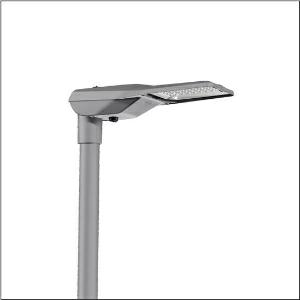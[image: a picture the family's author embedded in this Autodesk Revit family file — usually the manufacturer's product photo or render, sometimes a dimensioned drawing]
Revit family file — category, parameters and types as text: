
# Revit family: streetlight_sl_21_iq_mini___st1_0a_5xe2d41y08jb_7656
name_source: partatom
category: Lighting Fixtures
units: mm (PartAtom-declared; Revit-internal decimal feet)

## family parameters
Cut with Voids When Loaded = No
Host = Face
Light Source = No
Part Type = Normal
Room Calculation Point = No
Round Connector Dimension = Use Diameter
Shared = No

## types (1)
- --- (1 x LED, 11600 lm, 72.5 W, 4000K)
    Apparent Load = 73 VA
    CIE Flux Codes = 40 73 97 100 100
    Color Rendering = 70
    Color Temperature = 4000K
    Default Elevation = 1800 mm
    Description = Streetlight SL 21 iQ mini, mast luminaire, primary light control with lens, of PMMA, primary optical cover: cover, of toughened safety glass, transparent, light distribution: ST1.0a, light emission: direct distribution, primary light characteristic: asymmetric, installation type: post-top, side-entry, LED, High Power LED, rated luminous flux: 11.600lm, luminous efficacy: 160lm/W, light colour: 740, colour temperature: 4000K, control: presetting dimming logarithmic, Street-Remote, Auto-Match, Temp-Guard, Lumen-Switch, Night-Set, Smart-Wire, Light-Fading, Desk-Remote (wireless, voltage-free reading and setting of iQ features in the workshop via application-optimized NFC function/RFID function), optimised constant luminous flux control (CLO 2.0), mains connection: 220..240V, AC, 50/60Hz, start of lifetime: 73W, end of service life: 76W, reduction: 33W, luminaire housing, of diecast aluminium, powder-coated, Siteco® metallic grey (DB 702S), corrosivity category C5 mid according to DIN EN ISO 12944, please order mast flange separately, inclination adjustable: 0°, 5°, 10°, 15°, sealing non-destructively replaceable, multi-level sealing system, length: 628mm, width: 235mm, height: 110mm, mast flange for spigot size: 42mm (side-entry): 5XC10008XM4, 60/48mm (side-entry/post-top): 5XC10108XM2, 76/60mm (side-entry/post-top): 5XC10108XM1, Smart Interface below and above, protection rating (complete): IP66, insulation class (complete): insulation class II (safety insulation), certification: CE, ENEC, ENEC+, VDE, impact resistance: IK09, permissible operating ambient temperature for outdoor applications: -40..+50°C, standard-compliant lighting for roads and squares, packaging unit: 1 piece

Light Distribution: ST1.0a
    Height = 110 mm
    Lamp = 1 x LED
    Lamp Light Flux = 11600 lm
    Lamp Power = 72.5 W
    Lamp count = 1
    Length = 625 mm
    Luminous efficacy = 160 lm/W
    Manufacturer = Siteco
    ModVariant = No
    Model = 5XE2D41Y08JB
    Number of Poles = 1
    OnlyDefault = Yes
    Power Factor = 1
    Product Name = Streetlight SL 21 iQ mini | ST1.0a
    Product group = mast luminaire | pylon top
    ProductGroupID = 6100
    Protection Class = Protection class II
    Protection Degree = IP 66
    RLX_Detail_Level = 1
    RLX_Emergency_Light_Flux = 0 lm
    RLX_Emergency_Type = 0
    RLX_Emergency_Type_DB = No
    RlxData = <blob elided: 92749 chars, md5=e1f4e0a2>
    Socket = socket
    Standby Power = 0 W
    System Light Flux = 11600 lm
    System Power = 73 W
    Type Comments = factory setting: luminous flux: 100 % | dim-lin: 254 | 755 mA
    Type Image = l_1003514.jpg
    URL = http://relux.com
    VarID = @adj_044035
    Voltage = 0 V
    Weight = 0.00 kg
    Width = 234 mm

## geometry (parser evidence)
native form markers: Blend x4, Sweep x12
no freeform markers — native parametric forms only
